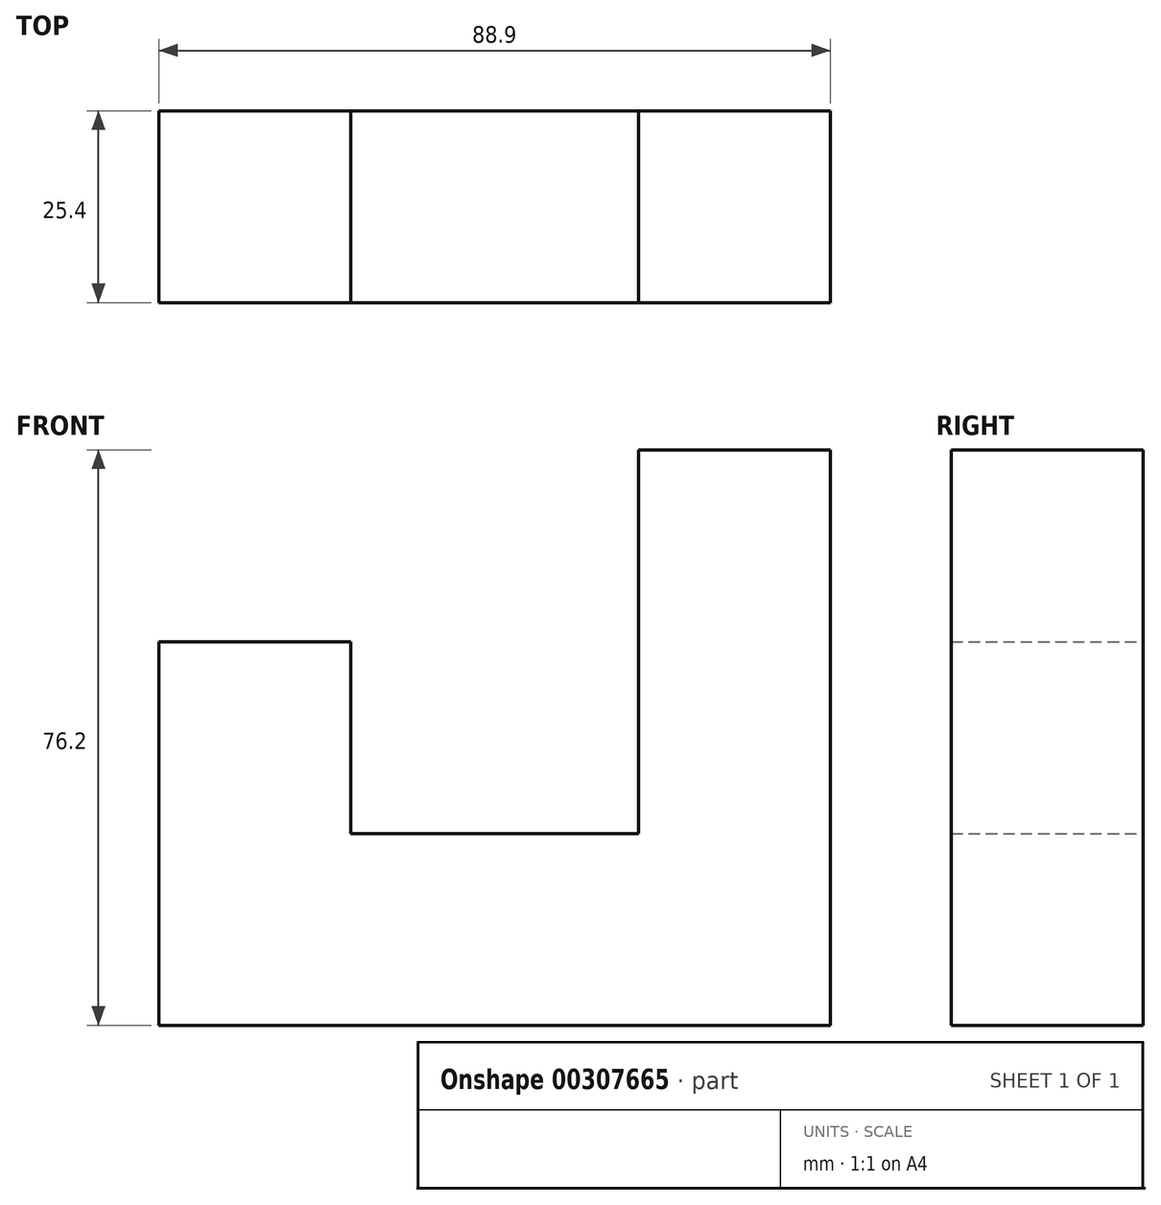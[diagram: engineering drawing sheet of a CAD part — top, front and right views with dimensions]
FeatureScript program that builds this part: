
annotation { "Feature Type Name" : "Feature", "Feature Type Description" : "" }
export const myFeature = defineFeature(function(context is Context, id is Id, definition is map)
    precondition{}
    {
        {
            var Q0;
            Q0=qCreatedBy(makeId("Front.planeOp"),FACE);
            var sketch = newSketch(context, id + "F0", { "sketchPlane" : qUnion([Q0])});
            skLineSegment(sketch, "E0", {"start": v(-55.9, -34.4) * mm, "end": v(33, -34.4) * mm});
            skLineSegment(sketch, "E1", {"start": v(33, -34.4) * mm, "end": v(33, 41.8) * mm});
            skLineSegment(sketch, "E2", {"start": v(33, 41.8) * mm, "end": v(7.6, 41.8) * mm});
            skLineSegment(sketch, "E3", {"start": v(7.6, 41.8) * mm, "end": v(7.6, -9) * mm});
            skLineSegment(sketch, "E4", {"start": v(7.6, -9) * mm, "end": v(-30.5, -9) * mm});
            skLineSegment(sketch, "E5", {"start": v(-30.5, -9) * mm, "end": v(-30.5, 16.4) * mm});
            skLineSegment(sketch, "E6", {"start": v(-30.5, 16.4) * mm, "end": v(-55.9, 16.4) * mm});
            skLineSegment(sketch, "E7", {"start": v(-55.9, 16.4) * mm, "end": v(-55.9, -34.4) * mm});
            skSolve(sketch);
        }
        {
            var Q0;
            Q0=makeQuery(id+"F0.imprint","IMPRINT",FACE,{"disambiguationData":[TD([[makeQuery(id+"F0.imprint","IMPRINT",EDGE,{"derivedFrom":sQuery(id+"F0.wireOp",EDGE,"E0")}),1.0]])]});
            extrude(context, id + "F1", {"entities" : qUnion([Q0]), "depth" : 25.4 * mm});
        }
    });
